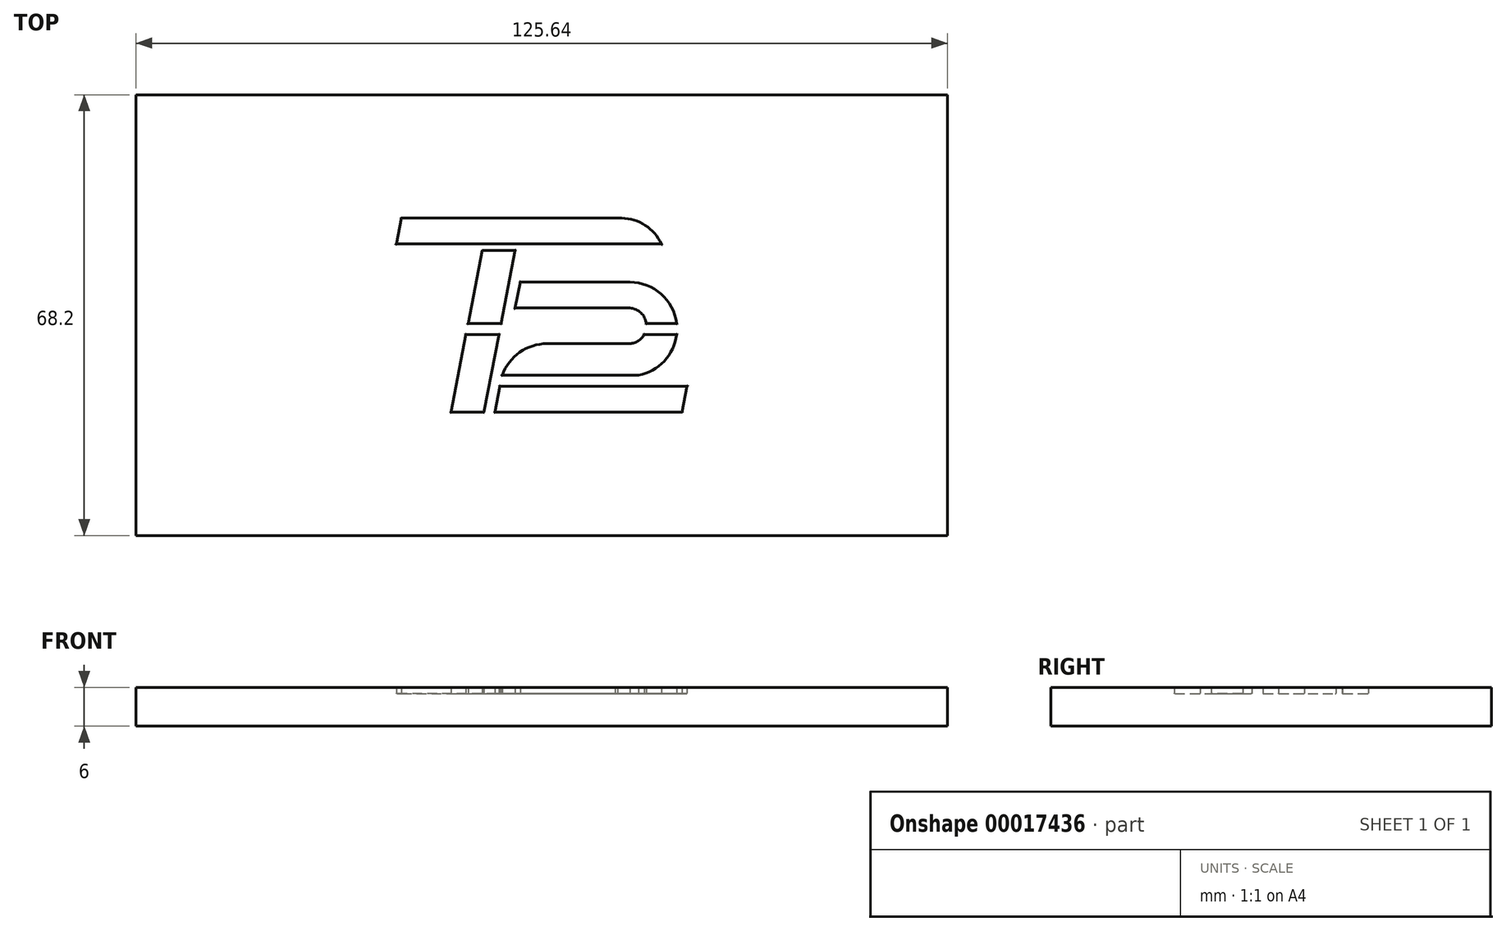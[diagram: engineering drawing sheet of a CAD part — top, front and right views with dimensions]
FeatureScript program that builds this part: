
annotation { "Feature Type Name" : "Feature", "Feature Type Description" : "" }
export const myFeature = defineFeature(function(context is Context, id is Id, definition is map)
    precondition{}
    {
        {
            var Q0;
            Q0=qCreatedBy(makeId("Top.planeOp"),FACE);
            var sketch = newSketch(context, id + "F0", { "sketchPlane" : qUnion([Q0])});
            skLineSegment(sketch, "E0.rect.bottom", {"start": v(22.5, 15) * mm, "end": v(-22.5, 15) * mm, "construction": true});
            skLineSegment(sketch, "E0.rect.top", {"start": v(22.5, -15) * mm, "end": v(-22.5, -15) * mm, "construction": true});
            skLineSegment(sketch, "E0.rect.left", {"start": v(22.5, 15) * mm, "end": v(22.5, -15) * mm, "construction": true});
            skLineSegment(sketch, "E0.rect.right", {"start": v(-22.5, 15) * mm, "end": v(-22.5, -15) * mm, "construction": true});
            skPoint(sketch, "E0.rect.middle", {"position": v(0, 0) * mm});
            skLineSegment(sketch, "E1", {"start": v(-14.06, -15) * mm, "end": v(-9.2, 10) * mm});
            skLineSegment(sketch, "E2.0", {"start": v(-9.15, -15.95) * mm, "end": v(-6.64, -3) * mm});
            skLineSegment(sketch, "E3", {"start": v(-14.06, -15) * mm, "end": v(-8.97, -15) * mm});
            skLineSegment(sketch, "E4.0", {"start": v(22.5, 11) * mm, "end": v(-22.5, 11) * mm});
            skLineSegment(sketch, "E5.0", {"start": v(-4.1, 10) * mm, "end": v(-9.2, 10) * mm});
            skLineSegment(sketch, "E6", {"start": v(-22.5, 11) * mm, "end": v(-21.72, 15) * mm});
            skLineSegment(sketch, "E7", {"start": v(-21.72, 15) * mm, "end": v(12.36, 15) * mm});
            skArc(sketch, "E8", {"start": v(12.36, 15) * mm, "mid": v(18.28, 11.47) * mm, "end": v(17.99, 4.58) * mm});
            skArc(sketch, "E9.0", {"start": v(12.36, 11) * mm, "mid": v(15.01, 8.92) * mm, "end": v(13.63, 5.85) * mm, "construction": true});
            skLineSegment(sketch, "E10", {"start": v(-11.73, -3) * mm, "end": v(-6.64, -3) * mm});
            skLineSegment(sketch, "E11", {"start": v(-11.4, -1.3) * mm, "end": v(-6.3, -1.3) * mm});
            skLineSegment(sketch, "E12.trimOffspring", {"start": v(-6.3, -1.3) * mm, "end": v(-4.1, 10) * mm});
            skLineSegment(sketch, "E13", {"start": v(-6.3, -1.3) * mm, "end": v(22.5, -1.3) * mm, "construction": true});
            skLineSegment(sketch, "E14.0", {"start": v(-7.24, -15) * mm, "end": v(-5.37, -5.41) * mm});
            skLineSegment(sketch, "E15", {"start": v(-3.33, 5.1) * mm, "end": v(13.65, 5.1) * mm});
            skLineSegment(sketch, "E16.0", {"start": v(-4.1, 1.1) * mm, "end": v(13.65, 1.1) * mm});
            skArc(sketch, "E17", {"start": v(13.65, 5.1) * mm, "mid": v(18.48, 3.27) * mm, "end": v(20.87, -1.3) * mm});
            skLineSegment(sketch, "E18", {"start": v(-7.24, -15) * mm, "end": v(22.5, -15) * mm});
            skLineSegment(sketch, "E19", {"start": v(21.72, -15) * mm, "end": v(22.5, -11) * mm});
            skLineSegment(sketch, "E20", {"start": v(22.5, -11) * mm, "end": v(-6.46, -11) * mm});
            skLineSegment(sketch, "E21.0", {"start": v(22.5, -9.3) * mm, "end": v(-6.38, -9.3) * mm});
            skLineSegment(sketch, "E22", {"start": v(13.45, -5.41) * mm, "end": v(-5.37, -5.41) * mm, "construction": true});
            skLineSegment(sketch, "E23", {"start": v(-4.1, 1.1) * mm, "end": v(-2.44, 9.68) * mm});
            skArc(sketch, "E24.0", {"start": v(13.63, 5.85) * mm, "mid": v(15.9, 5.53) * mm, "end": v(17.99, 4.58) * mm});
            skArc(sketch, "E25", {"start": v(17.99, 4.58) * mm, "mid": v(21.51, -3.7) * mm, "end": v(15.1, -10.04) * mm, "construction": true});
            skLineSegment(sketch, "E26", {"start": v(16.19, -1.3) * mm, "end": v(20.87, -1.3) * mm});
            skLineSegment(sketch, "E27.0", {"start": v(15.86, -3) * mm, "end": v(20.87, -3) * mm});
            skArc(sketch, "E28", {"start": v(20.87, -1.3) * mm, "mid": v(20.92, -2.15) * mm, "end": v(20.87, -3) * mm, "construction": true});
            skArc(sketch, "E29", {"start": v(20.87, -3) * mm, "mid": v(18.96, -7.12) * mm, "end": v(14.97, -9.3) * mm});
            skLineSegment(sketch, "E30.0", {"start": v(13.45, -4.41) * mm, "end": v(0.85, -4.41) * mm});
            skLineSegment(sketch, "E31", {"start": v(-5.37, -5.41) * mm, "end": v(-5.18, -4.41) * mm});
            skArc(sketch, "E32", {"start": v(13.45, -4.41) * mm, "mid": v(16.2, -1.75) * mm, "end": v(13.65, 1.1) * mm});
            skLineSegment(sketch, "E33", {"start": v(13.65, 1.1) * mm, "end": v(22.5, 1.1) * mm, "construction": true});
            skLineSegment(sketch, "E34", {"start": v(0.85, -4.41) * mm, "end": v(-5.18, -4.41) * mm, "construction": true});
            skArc(sketch, "E35", {"start": v(0.85, -4.41) * mm, "mid": v(-3.41, -5.76) * mm, "end": v(-6.13, -9.3) * mm});
            skArc(sketch, "E36", {"start": v(13.63, 5.85) * mm, "mid": v(14.3, 9.2) * mm, "end": v(11.39, 11) * mm});
            skSolve(sketch);
        }
        {
            var Q0;
            {var subQ7=sQuery(id+"F0.wireOp",EDGE,"E6");Q0=makeQuery(id+"F0.imprint","IMPRINT",FACE,{"disambiguationData":[TD([[makeQuery(id+"F0.imprint","IMPRINT",EDGE,{"derivedFrom":subQ7}),-1.0]])]});}
            var Q1;
            {var subQ3=sQuery(id+"F0.wireOp",EDGE,"E24.0");Q1=makeQuery(id+"F0.imprint","IMPRINT",FACE,{"disambiguationData":[TD([[makeQuery(id+"F0.imprint","IMPRINT",EDGE,{"derivedFrom":subQ3}),1.0]])]});}
            var Q2;
            {var subQ1=sQuery(id+"F0.wireOp",EDGE,"E5.0");Q2=makeQuery(id+"F0.imprint","IMPRINT",FACE,{"disambiguationData":[TD([[makeQuery(id+"F0.imprint","IMPRINT",EDGE,{"derivedFrom":subQ1}),1.0]])]});}
            var Q3;
            {var subQ1=sQuery(id+"F0.wireOp",EDGE,"E3");Q3=makeQuery(id+"F0.imprint","IMPRINT",FACE,{"disambiguationData":[TD([[makeQuery(id+"F0.imprint","IMPRINT",EDGE,{"derivedFrom":subQ1}),1.0]])]});}
            var Q4;
            {var subQ4=sQuery(id+"F0.wireOp",EDGE,"E15");Q4=makeQuery(id+"F0.imprint","IMPRINT",FACE,{"disambiguationData":[TD([[makeQuery(id+"F0.imprint","IMPRINT",EDGE,{"derivedFrom":subQ4}),-1.0]])]});}
            var Q5;
            {var subQ3=sQuery(id+"F0.wireOp",EDGE,"E27.0");Q5=makeQuery(id+"F0.imprint","IMPRINT",FACE,{"disambiguationData":[TD([[makeQuery(id+"F0.imprint","IMPRINT",EDGE,{"derivedFrom":subQ3}),-1.0]])]});}
            var Q6;
            {var subQ1=sQuery(id+"F0.wireOp",EDGE,"E19");Q6=makeQuery(id+"F0.imprint","IMPRINT",FACE,{"disambiguationData":[TD([[makeQuery(id+"F0.imprint","IMPRINT",EDGE,{"derivedFrom":subQ1}),1.0]])]});}
            extrude(context, id + "F1", {"entities" : qUnion([Q0, Q1, Q2, Q3, Q4, Q5, Q6]), "depth" : 5 * mm});
        }
        {
            var Q0;
            Q0=qCreatedBy(makeId("Top.planeOp"),FACE);
            var sketch = newSketch(context, id + "F2", { "sketchPlane" : qUnion([Q0])});
            skLineSegment(sketch, "E37.rect.bottom", {"start": v(62.82, 34.1) * mm, "end": v(-62.82, 34.1) * mm});
            skLineSegment(sketch, "E37.rect.top", {"start": v(62.82, -34.1) * mm, "end": v(-62.82, -34.1) * mm});
            skLineSegment(sketch, "E37.rect.left", {"start": v(62.82, 34.1) * mm, "end": v(62.82, -34.1) * mm});
            skLineSegment(sketch, "E37.rect.right", {"start": v(-62.82, 34.1) * mm, "end": v(-62.82, -34.1) * mm});
            skPoint(sketch, "E37.rect.middle", {"position": v(0, 0) * mm});
            skSolve(sketch);
        }
        {
            var Q0;
            Q0 = qSketchRegion(id + "F2", true);
            extrude(context, id + "F3", {"entities" : qUnion([Q0]), "depth" : 1 * mm, "hasSecondDirection" : true, "secondDirectionOppositeDirection" : true, "secondDirectionDepth" : 5 * mm});
        }
        {
            var Q0;
            Q0=makeQuery(id+"F1.opExtrude","SWEPT_BODY",BODY,{"disambiguationData":[OSD([sQuery(id+"F0.wireOp",EDGE,"E1"),sQuery(id+"F0.wireOp",EDGE,"E2.0"),sQuery(id+"F0.wireOp",EDGE,"E3"),sQuery(id+"F0.wireOp",EDGE,"E10")])]});
            var Q1;
            Q1=makeQuery(id+"F1.opExtrude","SWEPT_BODY",BODY,{"disambiguationData":[OSD([sQuery(id+"F0.wireOp",EDGE,"E1"),sQuery(id+"F0.wireOp",EDGE,"E5.0"),sQuery(id+"F0.wireOp",EDGE,"E11"),sQuery(id+"F0.wireOp",EDGE,"E12.trimOffspring")])]});
            var Q2;
            Q2=makeQuery(id+"F1.opExtrude","SWEPT_BODY",BODY,{"disambiguationData":[OSD([sQuery(id+"F0.wireOp",EDGE,"E4.0"),sQuery(id+"F0.wireOp",EDGE,"E6"),sQuery(id+"F0.wireOp",EDGE,"E7"),sQuery(id+"F0.wireOp",EDGE,"E8"),sQuery(id+"F0.wireOp",EDGE,"E24.0"),sQuery(id+"F0.wireOp",EDGE,"E36")])]});
            var Q3;
            Q3=makeQuery(id+"F1.opExtrude","SWEPT_BODY",BODY,{"disambiguationData":[OSD([sQuery(id+"F0.wireOp",EDGE,"E15"),sQuery(id+"F0.wireOp",EDGE,"E16.0"),sQuery(id+"F0.wireOp",EDGE,"E17"),sQuery(id+"F0.wireOp",EDGE,"E23"),sQuery(id+"F0.wireOp",EDGE,"E26"),sQuery(id+"F0.wireOp",EDGE,"E32")])]});
            var Q4;
            Q4=makeQuery(id+"F1.opExtrude","SWEPT_BODY",BODY,{"disambiguationData":[OSD([sQuery(id+"F0.wireOp",EDGE,"E21.0"),sQuery(id+"F0.wireOp",EDGE,"E27.0"),sQuery(id+"F0.wireOp",EDGE,"E29"),sQuery(id+"F0.wireOp",EDGE,"E30.0"),sQuery(id+"F0.wireOp",EDGE,"E32"),sQuery(id+"F0.wireOp",EDGE,"E35")])]});
            var Q5;
            Q5=makeQuery(id+"F1.opExtrude","SWEPT_BODY",BODY,{"disambiguationData":[OSD([sQuery(id+"F0.wireOp",EDGE,"E14.0"),sQuery(id+"F0.wireOp",EDGE,"E18"),sQuery(id+"F0.wireOp",EDGE,"E19"),sQuery(id+"F0.wireOp",EDGE,"E20")])]});
            var Q6;
            Q6=makeQuery(id+"F3.opExtrude","SWEPT_BODY",BODY,{"disambiguationData":[OSD([sQuery(id+"F2.wireOp",EDGE,"E37.rect.bottom"),sQuery(id+"F2.wireOp",EDGE,"E37.rect.top"),sQuery(id+"F2.wireOp",EDGE,"E37.rect.left"),sQuery(id+"F2.wireOp",EDGE,"E37.rect.right")])]});
            booleanBodies(context, id + "F4", {"operationType" : BooleanOperationType.SUBTRACTION, "tools" : qUnion([Q0, Q1, Q2, Q3, Q4, Q5]), "targets" : qUnion([Q6])});
        }
        {
            var Q0;
            Q0=makeQuery(id+"F4.opBoolean","INTERSECT",EDGE,{"derivedFrom":[makeQuery(id+"F1.opExtrude","SWEPT_FACE",FACE,{"disambiguationData":[OSD([sQuery(id+"F0.wireOp",EDGE,"E7")])]}),makeQuery(id+"F3.opExtrude","CAP_FACE",FACE,{"disambiguationData":[OSD([sQuery(id+"F2.wireOp",EDGE,"E37.rect.bottom"),sQuery(id+"F2.wireOp",EDGE,"E37.rect.top"),sQuery(id+"F2.wireOp",EDGE,"E37.rect.left"),sQuery(id+"F2.wireOp",EDGE,"E37.rect.right")])],"isStart":false})]});
            var Q1;
            Q1=makeQuery(id+"F4.opBoolean","INTERSECT",EDGE,{"derivedFrom":[makeQuery(id+"F1.opExtrude","SWEPT_FACE",FACE,{"disambiguationData":[OSD([sQuery(id+"F0.wireOp",EDGE,"E24.0")])]}),makeQuery(id+"F3.opExtrude","CAP_FACE",FACE,{"disambiguationData":[OSD([sQuery(id+"F2.wireOp",EDGE,"E37.rect.bottom"),sQuery(id+"F2.wireOp",EDGE,"E37.rect.top"),sQuery(id+"F2.wireOp",EDGE,"E37.rect.left"),sQuery(id+"F2.wireOp",EDGE,"E37.rect.right")])],"isStart":false})]});
            var Q2;
            Q2=makeQuery(id+"F4.opBoolean","INTERSECT",EDGE,{"derivedFrom":[makeQuery(id+"F1.opExtrude","SWEPT_FACE",FACE,{"disambiguationData":[OSD([sQuery(id+"F0.wireOp",EDGE,"E36")])]}),makeQuery(id+"F3.opExtrude","CAP_FACE",FACE,{"disambiguationData":[OSD([sQuery(id+"F2.wireOp",EDGE,"E37.rect.bottom"),sQuery(id+"F2.wireOp",EDGE,"E37.rect.top"),sQuery(id+"F2.wireOp",EDGE,"E37.rect.left"),sQuery(id+"F2.wireOp",EDGE,"E37.rect.right")])],"isStart":false})]});
            var Q3;
            Q3=makeQuery(id+"F4.opBoolean","INTERSECT",EDGE,{"derivedFrom":[makeQuery(id+"F1.opExtrude","SWEPT_FACE",FACE,{"disambiguationData":[OSD([sQuery(id+"F0.wireOp",EDGE,"E6")])]}),makeQuery(id+"F3.opExtrude","CAP_FACE",FACE,{"disambiguationData":[OSD([sQuery(id+"F2.wireOp",EDGE,"E37.rect.bottom"),sQuery(id+"F2.wireOp",EDGE,"E37.rect.top"),sQuery(id+"F2.wireOp",EDGE,"E37.rect.left"),sQuery(id+"F2.wireOp",EDGE,"E37.rect.right")])],"isStart":false})]});
            var Q4;
            Q4=makeQuery(id+"F4.opBoolean","INTERSECT",EDGE,{"derivedFrom":[makeQuery(id+"F1.opExtrude","SWEPT_FACE",FACE,{"disambiguationData":[OSD([sQuery(id+"F0.wireOp",EDGE,"E5.0")])]}),makeQuery(id+"F3.opExtrude","CAP_FACE",FACE,{"disambiguationData":[OSD([sQuery(id+"F2.wireOp",EDGE,"E37.rect.bottom"),sQuery(id+"F2.wireOp",EDGE,"E37.rect.top"),sQuery(id+"F2.wireOp",EDGE,"E37.rect.left"),sQuery(id+"F2.wireOp",EDGE,"E37.rect.right")])],"isStart":false})]});
            var Q5;
            Q5=makeQuery(id+"F4.opBoolean","INTERSECT",EDGE,{"derivedFrom":[makeQuery(id+"F1.opExtrude","SWEPT_FACE",FACE,{"disambiguationData":[OSD([sQuery(id+"F0.wireOp",EDGE,"E12.trimOffspring")])]}),makeQuery(id+"F3.opExtrude","CAP_FACE",FACE,{"disambiguationData":[OSD([sQuery(id+"F2.wireOp",EDGE,"E37.rect.bottom"),sQuery(id+"F2.wireOp",EDGE,"E37.rect.top"),sQuery(id+"F2.wireOp",EDGE,"E37.rect.left"),sQuery(id+"F2.wireOp",EDGE,"E37.rect.right")])],"isStart":false})]});
            var Q6;
            Q6=makeQuery(id+"F4.opBoolean","INTERSECT",EDGE,{"derivedFrom":[makeQuery(id+"F1.opExtrude","SWEPT_FACE",FACE,{"disambiguationData":[OSD([sQuery(id+"F0.wireOp",EDGE,"E11")])]}),makeQuery(id+"F3.opExtrude","CAP_FACE",FACE,{"disambiguationData":[OSD([sQuery(id+"F2.wireOp",EDGE,"E37.rect.bottom"),sQuery(id+"F2.wireOp",EDGE,"E37.rect.top"),sQuery(id+"F2.wireOp",EDGE,"E37.rect.left"),sQuery(id+"F2.wireOp",EDGE,"E37.rect.right")])],"isStart":false})]});
            var Q7;
            {var subQ0=sQuery(id+"F0.wireOp",EDGE,"E1");Q7=makeQuery(id+"F4.opBoolean","INTERSECT",EDGE,{"derivedFrom":[makeQuery(id+"F1.opExtrude","SWEPT_FACE",FACE,{"disambiguationData":[OSD([subQ0]),TDD([makeQuery(id+"F0.imprint","IMPRINT",EDGE,{"disambiguationData":[TD([[makeQuery(id+"F0.imprint","INTERSECT",VERTEX,{"derivedFrom":[subQ0,sQuery(id+"F0.wireOp",EDGE,"E5.0")]}),1.0]])],"derivedFrom":subQ0})])]}),makeQuery(id+"F3.opExtrude","CAP_FACE",FACE,{"disambiguationData":[OSD([sQuery(id+"F2.wireOp",EDGE,"E37.rect.bottom"),sQuery(id+"F2.wireOp",EDGE,"E37.rect.top"),sQuery(id+"F2.wireOp",EDGE,"E37.rect.left"),sQuery(id+"F2.wireOp",EDGE,"E37.rect.right")])],"isStart":false})]});}
            var Q8;
            Q8=makeQuery(id+"F4.opBoolean","INTERSECT",EDGE,{"derivedFrom":[makeQuery(id+"F1.opExtrude","SWEPT_FACE",FACE,{"disambiguationData":[OSD([sQuery(id+"F0.wireOp",EDGE,"E10")])]}),makeQuery(id+"F3.opExtrude","CAP_FACE",FACE,{"disambiguationData":[OSD([sQuery(id+"F2.wireOp",EDGE,"E37.rect.bottom"),sQuery(id+"F2.wireOp",EDGE,"E37.rect.top"),sQuery(id+"F2.wireOp",EDGE,"E37.rect.left"),sQuery(id+"F2.wireOp",EDGE,"E37.rect.right")])],"isStart":false})]});
            var Q9;
            {var subQ0=sQuery(id+"F0.wireOp",EDGE,"E1");Q9=makeQuery(id+"F4.opBoolean","INTERSECT",EDGE,{"derivedFrom":[makeQuery(id+"F1.opExtrude","SWEPT_FACE",FACE,{"disambiguationData":[OSD([subQ0]),TDD([makeQuery(id+"F0.imprint","IMPRINT",EDGE,{"disambiguationData":[TD([[makeQuery(id+"F0.imprint","INTERSECT",VERTEX,{"derivedFrom":[subQ0,sQuery(id+"F0.wireOp",EDGE,"E3")]}),-1.0]])],"derivedFrom":subQ0})])]}),makeQuery(id+"F3.opExtrude","CAP_FACE",FACE,{"disambiguationData":[OSD([sQuery(id+"F2.wireOp",EDGE,"E37.rect.bottom"),sQuery(id+"F2.wireOp",EDGE,"E37.rect.top"),sQuery(id+"F2.wireOp",EDGE,"E37.rect.left"),sQuery(id+"F2.wireOp",EDGE,"E37.rect.right")])],"isStart":false})]});}
            var Q10;
            Q10=makeQuery(id+"F4.opBoolean","INTERSECT",EDGE,{"derivedFrom":[makeQuery(id+"F1.opExtrude","SWEPT_FACE",FACE,{"disambiguationData":[OSD([sQuery(id+"F0.wireOp",EDGE,"E3")])]}),makeQuery(id+"F3.opExtrude","CAP_FACE",FACE,{"disambiguationData":[OSD([sQuery(id+"F2.wireOp",EDGE,"E37.rect.bottom"),sQuery(id+"F2.wireOp",EDGE,"E37.rect.top"),sQuery(id+"F2.wireOp",EDGE,"E37.rect.left"),sQuery(id+"F2.wireOp",EDGE,"E37.rect.right")])],"isStart":false})]});
            var Q11;
            Q11=makeQuery(id+"F4.opBoolean","INTERSECT",EDGE,{"derivedFrom":[makeQuery(id+"F1.opExtrude","SWEPT_FACE",FACE,{"disambiguationData":[OSD([sQuery(id+"F0.wireOp",EDGE,"E2.0")])]}),makeQuery(id+"F3.opExtrude","CAP_FACE",FACE,{"disambiguationData":[OSD([sQuery(id+"F2.wireOp",EDGE,"E37.rect.bottom"),sQuery(id+"F2.wireOp",EDGE,"E37.rect.top"),sQuery(id+"F2.wireOp",EDGE,"E37.rect.left"),sQuery(id+"F2.wireOp",EDGE,"E37.rect.right")])],"isStart":false})]});
            var Q12;
            Q12=makeQuery(id+"F4.opBoolean","INTERSECT",EDGE,{"derivedFrom":[makeQuery(id+"F1.opExtrude","SWEPT_FACE",FACE,{"disambiguationData":[OSD([sQuery(id+"F0.wireOp",EDGE,"E15")])]}),makeQuery(id+"F3.opExtrude","CAP_FACE",FACE,{"disambiguationData":[OSD([sQuery(id+"F2.wireOp",EDGE,"E37.rect.bottom"),sQuery(id+"F2.wireOp",EDGE,"E37.rect.top"),sQuery(id+"F2.wireOp",EDGE,"E37.rect.left"),sQuery(id+"F2.wireOp",EDGE,"E37.rect.right")])],"isStart":false})]});
            var Q13;
            Q13=makeQuery(id+"F4.opBoolean","INTERSECT",EDGE,{"derivedFrom":[makeQuery(id+"F1.opExtrude","SWEPT_FACE",FACE,{"disambiguationData":[OSD([sQuery(id+"F0.wireOp",EDGE,"E26")])]}),makeQuery(id+"F3.opExtrude","CAP_FACE",FACE,{"disambiguationData":[OSD([sQuery(id+"F2.wireOp",EDGE,"E37.rect.bottom"),sQuery(id+"F2.wireOp",EDGE,"E37.rect.top"),sQuery(id+"F2.wireOp",EDGE,"E37.rect.left"),sQuery(id+"F2.wireOp",EDGE,"E37.rect.right")])],"isStart":false})]});
            var Q14;
            {var subQ0=sQuery(id+"F0.wireOp",EDGE,"E32");Q14=makeQuery(id+"F4.opBoolean","INTERSECT",EDGE,{"derivedFrom":[makeQuery(id+"F1.opExtrude","SWEPT_FACE",FACE,{"disambiguationData":[OSD([subQ0]),TDD([makeQuery(id+"F0.imprint","IMPRINT",EDGE,{"disambiguationData":[TD([[makeQuery(id+"F0.imprint","INTERSECT",VERTEX,{"derivedFrom":[sQuery(id+"F0.wireOp",EDGE,"E16.0"),subQ0]}),1.0]])],"derivedFrom":subQ0})])]}),makeQuery(id+"F3.opExtrude","CAP_FACE",FACE,{"disambiguationData":[OSD([sQuery(id+"F2.wireOp",EDGE,"E37.rect.bottom"),sQuery(id+"F2.wireOp",EDGE,"E37.rect.top"),sQuery(id+"F2.wireOp",EDGE,"E37.rect.left"),sQuery(id+"F2.wireOp",EDGE,"E37.rect.right")])],"isStart":false})]});}
            var Q15;
            Q15=makeQuery(id+"F4.opBoolean","INTERSECT",EDGE,{"derivedFrom":[makeQuery(id+"F1.opExtrude","SWEPT_FACE",FACE,{"disambiguationData":[OSD([sQuery(id+"F0.wireOp",EDGE,"E16.0")])]}),makeQuery(id+"F3.opExtrude","CAP_FACE",FACE,{"disambiguationData":[OSD([sQuery(id+"F2.wireOp",EDGE,"E37.rect.bottom"),sQuery(id+"F2.wireOp",EDGE,"E37.rect.top"),sQuery(id+"F2.wireOp",EDGE,"E37.rect.left"),sQuery(id+"F2.wireOp",EDGE,"E37.rect.right")])],"isStart":false})]});
            var Q16;
            Q16=makeQuery(id+"F4.opBoolean","INTERSECT",EDGE,{"derivedFrom":[makeQuery(id+"F1.opExtrude","SWEPT_FACE",FACE,{"disambiguationData":[OSD([sQuery(id+"F0.wireOp",EDGE,"E23")])]}),makeQuery(id+"F3.opExtrude","CAP_FACE",FACE,{"disambiguationData":[OSD([sQuery(id+"F2.wireOp",EDGE,"E37.rect.bottom"),sQuery(id+"F2.wireOp",EDGE,"E37.rect.top"),sQuery(id+"F2.wireOp",EDGE,"E37.rect.left"),sQuery(id+"F2.wireOp",EDGE,"E37.rect.right")])],"isStart":false})]});
            var Q17;
            Q17=makeQuery(id+"F4.opBoolean","INTERSECT",EDGE,{"derivedFrom":[makeQuery(id+"F1.opExtrude","SWEPT_FACE",FACE,{"disambiguationData":[OSD([sQuery(id+"F0.wireOp",EDGE,"E27.0")])]}),makeQuery(id+"F3.opExtrude","CAP_FACE",FACE,{"disambiguationData":[OSD([sQuery(id+"F2.wireOp",EDGE,"E37.rect.bottom"),sQuery(id+"F2.wireOp",EDGE,"E37.rect.top"),sQuery(id+"F2.wireOp",EDGE,"E37.rect.left"),sQuery(id+"F2.wireOp",EDGE,"E37.rect.right")])],"isStart":false})]});
            var Q18;
            {var subQ0=sQuery(id+"F0.wireOp",EDGE,"E32");Q18=makeQuery(id+"F4.opBoolean","INTERSECT",EDGE,{"derivedFrom":[makeQuery(id+"F1.opExtrude","SWEPT_FACE",FACE,{"disambiguationData":[OSD([subQ0]),TDD([makeQuery(id+"F0.imprint","IMPRINT",EDGE,{"disambiguationData":[TD([[makeQuery(id+"F0.imprint","INTERSECT",VERTEX,{"derivedFrom":[sQuery(id+"F0.wireOp",EDGE,"E27.0"),subQ0]}),1.0]])],"derivedFrom":subQ0})])]}),makeQuery(id+"F3.opExtrude","CAP_FACE",FACE,{"disambiguationData":[OSD([sQuery(id+"F2.wireOp",EDGE,"E37.rect.bottom"),sQuery(id+"F2.wireOp",EDGE,"E37.rect.top"),sQuery(id+"F2.wireOp",EDGE,"E37.rect.left"),sQuery(id+"F2.wireOp",EDGE,"E37.rect.right")])],"isStart":false})]});}
            var Q19;
            Q19=makeQuery(id+"F4.opBoolean","INTERSECT",EDGE,{"derivedFrom":[makeQuery(id+"F1.opExtrude","SWEPT_FACE",FACE,{"disambiguationData":[OSD([sQuery(id+"F0.wireOp",EDGE,"E21.0")])]}),makeQuery(id+"F3.opExtrude","CAP_FACE",FACE,{"disambiguationData":[OSD([sQuery(id+"F2.wireOp",EDGE,"E37.rect.bottom"),sQuery(id+"F2.wireOp",EDGE,"E37.rect.top"),sQuery(id+"F2.wireOp",EDGE,"E37.rect.left"),sQuery(id+"F2.wireOp",EDGE,"E37.rect.right")])],"isStart":false})]});
            var Q20;
            Q20=makeQuery(id+"F4.opBoolean","INTERSECT",EDGE,{"derivedFrom":[makeQuery(id+"F1.opExtrude","SWEPT_FACE",FACE,{"disambiguationData":[OSD([sQuery(id+"F0.wireOp",EDGE,"E29")])]}),makeQuery(id+"F3.opExtrude","CAP_FACE",FACE,{"disambiguationData":[OSD([sQuery(id+"F2.wireOp",EDGE,"E37.rect.bottom"),sQuery(id+"F2.wireOp",EDGE,"E37.rect.top"),sQuery(id+"F2.wireOp",EDGE,"E37.rect.left"),sQuery(id+"F2.wireOp",EDGE,"E37.rect.right")])],"isStart":false})]});
            var Q21;
            Q21=makeQuery(id+"F4.opBoolean","INTERSECT",EDGE,{"derivedFrom":[makeQuery(id+"F1.opExtrude","SWEPT_FACE",FACE,{"disambiguationData":[OSD([sQuery(id+"F0.wireOp",EDGE,"E20")])]}),makeQuery(id+"F3.opExtrude","CAP_FACE",FACE,{"disambiguationData":[OSD([sQuery(id+"F2.wireOp",EDGE,"E37.rect.bottom"),sQuery(id+"F2.wireOp",EDGE,"E37.rect.top"),sQuery(id+"F2.wireOp",EDGE,"E37.rect.left"),sQuery(id+"F2.wireOp",EDGE,"E37.rect.right")])],"isStart":false})]});
            var Q22;
            Q22=makeQuery(id+"F4.opBoolean","INTERSECT",EDGE,{"derivedFrom":[makeQuery(id+"F1.opExtrude","SWEPT_FACE",FACE,{"disambiguationData":[OSD([sQuery(id+"F0.wireOp",EDGE,"E14.0")])]}),makeQuery(id+"F3.opExtrude","CAP_FACE",FACE,{"disambiguationData":[OSD([sQuery(id+"F2.wireOp",EDGE,"E37.rect.bottom"),sQuery(id+"F2.wireOp",EDGE,"E37.rect.top"),sQuery(id+"F2.wireOp",EDGE,"E37.rect.left"),sQuery(id+"F2.wireOp",EDGE,"E37.rect.right")])],"isStart":false})]});
            var Q23;
            Q23=makeQuery(id+"F4.opBoolean","INTERSECT",EDGE,{"derivedFrom":[makeQuery(id+"F1.opExtrude","SWEPT_FACE",FACE,{"disambiguationData":[OSD([sQuery(id+"F0.wireOp",EDGE,"E18")])]}),makeQuery(id+"F3.opExtrude","CAP_FACE",FACE,{"disambiguationData":[OSD([sQuery(id+"F2.wireOp",EDGE,"E37.rect.bottom"),sQuery(id+"F2.wireOp",EDGE,"E37.rect.top"),sQuery(id+"F2.wireOp",EDGE,"E37.rect.left"),sQuery(id+"F2.wireOp",EDGE,"E37.rect.right")])],"isStart":false})]});
            var Q24;
            Q24=makeQuery(id+"F4.opBoolean","INTERSECT",EDGE,{"derivedFrom":[makeQuery(id+"F1.opExtrude","SWEPT_FACE",FACE,{"disambiguationData":[OSD([sQuery(id+"F0.wireOp",EDGE,"E19")])]}),makeQuery(id+"F3.opExtrude","CAP_FACE",FACE,{"disambiguationData":[OSD([sQuery(id+"F2.wireOp",EDGE,"E37.rect.bottom"),sQuery(id+"F2.wireOp",EDGE,"E37.rect.top"),sQuery(id+"F2.wireOp",EDGE,"E37.rect.left"),sQuery(id+"F2.wireOp",EDGE,"E37.rect.right")])],"isStart":false})]});
            fillet(context, id + "F5", {"entities" : qUnion([Q0, Q1, Q2, Q3, Q4, Q5, Q6, Q7, Q8, Q9, Q10, Q11, Q12, Q13, Q14, Q15, Q16, Q17, Q18, Q19, Q20, Q21, Q22, Q23, Q24]), "radius" : .1 * mm, "tangentPropagation" : true, "allowEdgeOverflow" : false});
        }
        {
            var Q0;
            Q0=makeQuery(id+"F4.opBoolean","COPY",FACE,{"derivedFrom":makeQuery(id+"F1.opExtrude","CAP_FACE",FACE,{"disambiguationData":[OSD([sQuery(id+"F0.wireOp",EDGE,"E4.0"),sQuery(id+"F0.wireOp",EDGE,"E6"),sQuery(id+"F0.wireOp",EDGE,"E7"),sQuery(id+"F0.wireOp",EDGE,"E8"),sQuery(id+"F0.wireOp",EDGE,"E24.0"),sQuery(id+"F0.wireOp",EDGE,"E36")])],"isStart":true})});
            var Q1;
            Q1=makeQuery(id+"F4.opBoolean","COPY",FACE,{"derivedFrom":makeQuery(id+"F1.opExtrude","CAP_FACE",FACE,{"disambiguationData":[OSD([sQuery(id+"F0.wireOp",EDGE,"E1"),sQuery(id+"F0.wireOp",EDGE,"E5.0"),sQuery(id+"F0.wireOp",EDGE,"E11"),sQuery(id+"F0.wireOp",EDGE,"E12.trimOffspring")])],"isStart":true})});
            var Q2;
            Q2=makeQuery(id+"F4.opBoolean","COPY",FACE,{"derivedFrom":makeQuery(id+"F1.opExtrude","CAP_FACE",FACE,{"disambiguationData":[OSD([sQuery(id+"F0.wireOp",EDGE,"E15"),sQuery(id+"F0.wireOp",EDGE,"E16.0"),sQuery(id+"F0.wireOp",EDGE,"E17"),sQuery(id+"F0.wireOp",EDGE,"E23"),sQuery(id+"F0.wireOp",EDGE,"E26"),sQuery(id+"F0.wireOp",EDGE,"E32")])],"isStart":true})});
            var Q3;
            Q3=makeQuery(id+"F4.opBoolean","COPY",FACE,{"derivedFrom":makeQuery(id+"F1.opExtrude","CAP_FACE",FACE,{"disambiguationData":[OSD([sQuery(id+"F0.wireOp",EDGE,"E1"),sQuery(id+"F0.wireOp",EDGE,"E2.0"),sQuery(id+"F0.wireOp",EDGE,"E3"),sQuery(id+"F0.wireOp",EDGE,"E10")])],"isStart":true})});
            var Q4;
            Q4=makeQuery(id+"F4.opBoolean","COPY",FACE,{"derivedFrom":makeQuery(id+"F1.opExtrude","CAP_FACE",FACE,{"disambiguationData":[OSD([sQuery(id+"F0.wireOp",EDGE,"E21.0"),sQuery(id+"F0.wireOp",EDGE,"E27.0"),sQuery(id+"F0.wireOp",EDGE,"E29"),sQuery(id+"F0.wireOp",EDGE,"E30.0"),sQuery(id+"F0.wireOp",EDGE,"E32"),sQuery(id+"F0.wireOp",EDGE,"E35")])],"isStart":true})});
            var Q5;
            Q5=makeQuery(id+"F4.opBoolean","COPY",FACE,{"derivedFrom":makeQuery(id+"F1.opExtrude","CAP_FACE",FACE,{"disambiguationData":[OSD([sQuery(id+"F0.wireOp",EDGE,"E14.0"),sQuery(id+"F0.wireOp",EDGE,"E18"),sQuery(id+"F0.wireOp",EDGE,"E19"),sQuery(id+"F0.wireOp",EDGE,"E20")])],"isStart":true})});
            fillet(context, id + "F6", {"entities" : qUnion([Q0, Q1, Q2, Q3, Q4, Q5]), "radius" : .1 * mm, "tangentPropagation" : true, "allowEdgeOverflow" : false});
        }
    });
